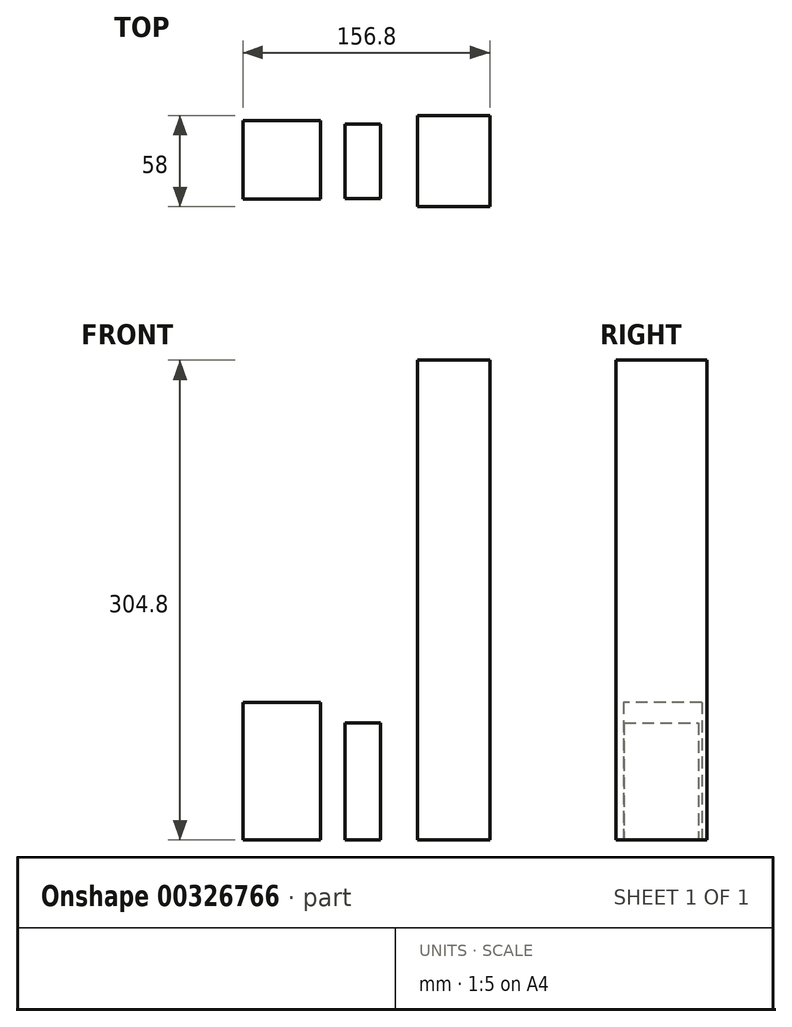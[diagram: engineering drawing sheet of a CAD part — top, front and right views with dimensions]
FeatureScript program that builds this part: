
annotation { "Feature Type Name" : "Feature", "Feature Type Description" : "" }
export const myFeature = defineFeature(function(context is Context, id is Id, definition is map)
    precondition{}
    {
        {
            var Q0;
            Q0=qCreatedBy(makeId("Top.planeOp"),FACE);
            var sketch = newSketch(context, id + "F0", { "sketchPlane" : qUnion([Q0])});
            skLineSegment(sketch, "E0.bottom", {"start": v(-121.2, 122.77) * mm, "end": v(-71.85, 122.77) * mm});
            skLineSegment(sketch, "E0.top", {"start": v(-121.2, 72.99) * mm, "end": v(-71.85, 72.99) * mm});
            skLineSegment(sketch, "E0.left", {"start": v(-121.2, 122.77) * mm, "end": v(-121.2, 72.99) * mm});
            skLineSegment(sketch, "E0.right", {"start": v(-71.85, 122.77) * mm, "end": v(-71.85, 72.99) * mm});
            skLineSegment(sketch, "E1.bottom", {"start": v(-56.4, 73.35) * mm, "end": v(-33.87, 73.35) * mm});
            skLineSegment(sketch, "E1.top", {"start": v(-56.4, 120.49) * mm, "end": v(-33.87, 120.49) * mm});
            skLineSegment(sketch, "E1.left", {"start": v(-56.4, 73.35) * mm, "end": v(-56.4, 120.49) * mm});
            skLineSegment(sketch, "E1.right", {"start": v(-33.87, 73.35) * mm, "end": v(-33.87, 120.49) * mm});
            skLineSegment(sketch, "E2.bottom", {"start": v(-10.43, 68.1) * mm, "end": v(35.6, 68.1) * mm});
            skLineSegment(sketch, "E2.top", {"start": v(-10.43, 126.1) * mm, "end": v(35.6, 126.1) * mm});
            skLineSegment(sketch, "E2.left", {"start": v(-10.43, 68.1) * mm, "end": v(-10.43, 126.1) * mm});
            skLineSegment(sketch, "E2.right", {"start": v(35.6, 68.1) * mm, "end": v(35.6, 126.1) * mm});
            skLineSegment(sketch, "E3.bottom", {"start": v(-35.87, 44.46) * mm, "end": v(18.36, 44.46) * mm});
            skLineSegment(sketch, "E3.top", {"start": v(-35.87, -60.84) * mm, "end": v(18.36, -60.84) * mm});
            skLineSegment(sketch, "E3.left", {"start": v(-35.87, 44.46) * mm, "end": v(-35.87, -60.84) * mm});
            skLineSegment(sketch, "E3.right", {"start": v(18.36, 44.46) * mm, "end": v(18.36, -60.84) * mm});
            skLineSegment(sketch, "E4.bottom", {"start": v(-113.4, 8.91) * mm, "end": v(-49.76, 8.91) * mm});
            skLineSegment(sketch, "E4.top", {"start": v(-113.4, -69.16) * mm, "end": v(-49.76, -69.16) * mm});
            skLineSegment(sketch, "E4.left", {"start": v(-113.4, 8.91) * mm, "end": v(-113.4, -69.16) * mm});
            skLineSegment(sketch, "E4.right", {"start": v(-49.76, 8.91) * mm, "end": v(-49.76, -69.16) * mm});
            skLineSegment(sketch, "E5.bottom", {"start": v(-12.98, -118.12) * mm, "end": v(75.47, -118.12) * mm});
            skLineSegment(sketch, "E5.top", {"start": v(-12.98, -89.38) * mm, "end": v(75.47, -89.38) * mm});
            skLineSegment(sketch, "E5.left", {"start": v(-12.98, -118.12) * mm, "end": v(-12.98, -89.38) * mm});
            skLineSegment(sketch, "E5.right", {"start": v(75.47, -118.12) * mm, "end": v(75.47, -89.38) * mm});
            skLineSegment(sketch, "E6.bottom", {"start": v(51.58, -63.14) * mm, "end": v(124.43, -63.14) * mm});
            skLineSegment(sketch, "E6.top", {"start": v(51.58, 11.53) * mm, "end": v(124.43, 11.53) * mm});
            skLineSegment(sketch, "E6.left", {"start": v(51.58, -63.14) * mm, "end": v(51.58, 11.53) * mm});
            skLineSegment(sketch, "E6.right", {"start": v(124.43, -63.14) * mm, "end": v(124.43, 11.53) * mm});
            skLineSegment(sketch, "E7.bottom", {"start": v(76.5, 58.16) * mm, "end": v(129.66, 58.16) * mm});
            skLineSegment(sketch, "E7.top", {"start": v(76.5, 115.18) * mm, "end": v(129.66, 115.18) * mm});
            skLineSegment(sketch, "E7.left", {"start": v(76.5, 58.16) * mm, "end": v(76.5, 115.18) * mm});
            skLineSegment(sketch, "E7.right", {"start": v(129.66, 58.16) * mm, "end": v(129.66, 115.18) * mm});
            skSolve(sketch);
        }
        {
            var Q0;
            Q0=makeQuery(id+"F0.imprint","IMPRINT",FACE,{"disambiguationData":[TD([[makeQuery(id+"F0.imprint","IMPRINT",EDGE,{"derivedFrom":sQuery(id+"F0.wireOp",EDGE,"E0.bottom")}),-1.0]])]});
            extrude(context, id + "F1", {"entities" : qUnion([Q0]), "depth" : 87.53 * mm});
        }
        {
            var Q0;
            Q0=makeQuery(id+"F0.imprint","IMPRINT",FACE,{"disambiguationData":[TD([[makeQuery(id+"F0.imprint","IMPRINT",EDGE,{"derivedFrom":sQuery(id+"F0.wireOp",EDGE,"E1.bottom")}),1.0]])]});
            extrude(context, id + "F2", {"entities" : qUnion([Q0]), "depth" : 74.46 * mm});
        }
        {
            var Q0;
            Q0=makeQuery(id+"F0.imprint","IMPRINT",FACE,{"disambiguationData":[TD([[makeQuery(id+"F0.imprint","IMPRINT",EDGE,{"derivedFrom":sQuery(id+"F0.wireOp",EDGE,"E2.bottom")}),1.0]])]});
            extrude(context, id + "F3", {"entities" : qUnion([Q0]), "depth" : 304.8 * mm});
        }
    });
